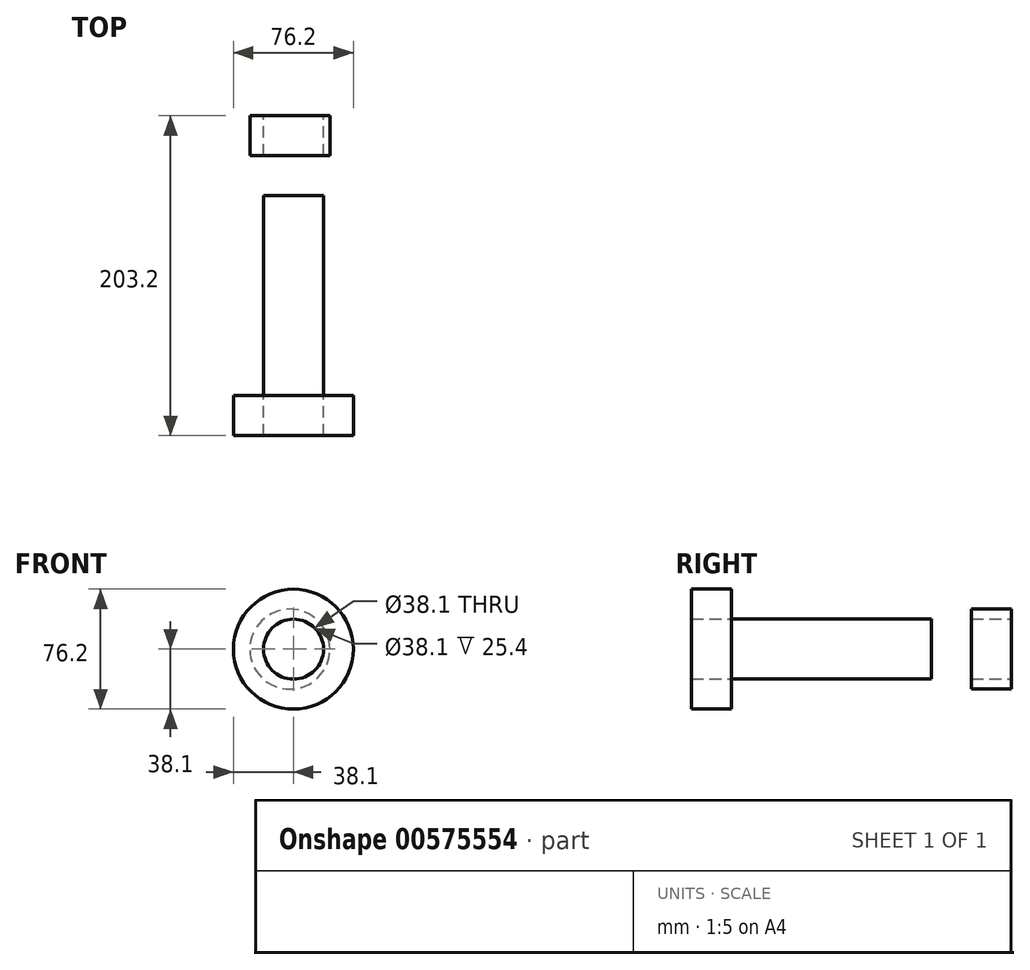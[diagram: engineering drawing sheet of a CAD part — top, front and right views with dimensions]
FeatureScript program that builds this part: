
annotation { "Feature Type Name" : "Feature", "Feature Type Description" : "" }
export const myFeature = defineFeature(function(context is Context, id is Id, definition is map)
    precondition{}
    {
        {
            var Q0;
            Q0=qCreatedBy(makeId("Front.planeOp"),FACE);
            var sketch = newSketch(context, id + "F0", { "sketchPlane" : qUnion([Q0])});
            skCircle(sketch, "E0", {"center": v(0, 0) * mm, "radius": 19.05 * mm});
            skSolve(sketch);
        }
        {
            var Q0;
            Q0=makeQuery(id+"F0.imprint","IMPRINT",FACE,{"disambiguationData":[TD([[makeQuery(id+"F0.imprint","IMPRINT",EDGE,{"derivedFrom":sQuery(id+"F0.wireOp",EDGE,"E0")}),1.0]])]});
            extrude(context, id + "F1", {"entities" : qUnion([Q0]), "depth" : 127 * mm, "offsetDistance" : 25.4 * mm});
        }
        {
            var Q0;
            Q0=makeQuery(id+"F1.opExtrude","CAP_FACE",FACE,{"disambiguationData":[OSD([sQuery(id+"F0.wireOp",EDGE,"E0")])],"isStart":true});
            cPlane(context, id + "F2", {"entities" : qUnion([Q0]), "cplaneType" : CPlaneType.OFFSET, "offset" : 25.4 * mm, "width" : 152.4 * mm, "height" : 152.4 * mm});
        }
        {
            var Q0;
            Q0=qCreatedBy(id+"F2.planeOp",FACE);
            var sketch = newSketch(context, id + "F3", { "sketchPlane" : qUnion([Q0])});
            skCircle(sketch, "E1", {"center": v(2.24, 0) * mm, "radius": 25.4 * mm});
            skSolve(sketch);
        }
        {
            var Q0;
            Q0=makeQuery(id+"F3.imprint","IMPRINT",FACE,{"disambiguationData":[TD([[makeQuery(id+"F3.imprint","IMPRINT",EDGE,{"derivedFrom":sQuery(id+"F3.wireOp",EDGE,"E1")}),1.0]])]});
            extrude(context, id + "F4", {"entities" : qUnion([Q0]), "depth" : 25.4 * mm, "offsetDistance" : 25.4 * mm});
        }
        {
            var Q0;
            Q0=makeQuery(id+"F4.opExtrude","CAP_FACE",FACE,{"disambiguationData":[OSD([sQuery(id+"F3.wireOp",EDGE,"E1")])],"isStart":false});
            var sketch = newSketch(context, id + "F5", { "sketchPlane" : qUnion([Q0])});
            skPoint(sketch, "E2", {"position": v(0, 0) * mm});
            skSolve(sketch);
        }
        {
            var Q0;
            Q0=sQuery(id+"F5.wireOp",VERTEX,"E2");
            var Q1;
            Q1=makeQuery(id+"F4.opExtrude","SWEPT_BODY",BODY,{"disambiguationData":[OSD([sQuery(id+"F3.wireOp",EDGE,"E1")])]});
            hole(context, id + "F6", {"style" : HoleStyle.SIMPLE, "endStyle" : HoleEndStyle.THROUGH, "holeDiameter" : 38.1 * mm, "isTappedThrough" : true, "tappedDepth" : 12.7 * mm, "tapClearance" : 3, "locations" : qUnion([Q0]), "scope" : qUnion([Q1])});
        }
        {
            var Q0;
            Q0=makeQuery(id+"F1.opExtrude","CAP_FACE",FACE,{"disambiguationData":[OSD([sQuery(id+"F0.wireOp",EDGE,"E0")])],"isStart":false});
            var sketch = newSketch(context, id + "F7", { "sketchPlane" : qUnion([Q0])});
            skCircle(sketch, "E3", {"center": v(0, 0) * mm, "radius": 38.1 * mm});
            skSolve(sketch);
        }
        {
            var Q0;
            Q0=makeQuery(id+"F7.imprint","IMPRINT",FACE,{"disambiguationData":[TD([[makeQuery(id+"F7.imprint","IMPRINT",EDGE,{"derivedFrom":sQuery(id+"F7.wireOp",EDGE,"E3")}),1.0]])]});
            extrude(context, id + "F8", {"entities" : qUnion([Q0]), "depth" : 25.4 * mm, "offsetDistance" : 25.4 * mm});
        }
    });
